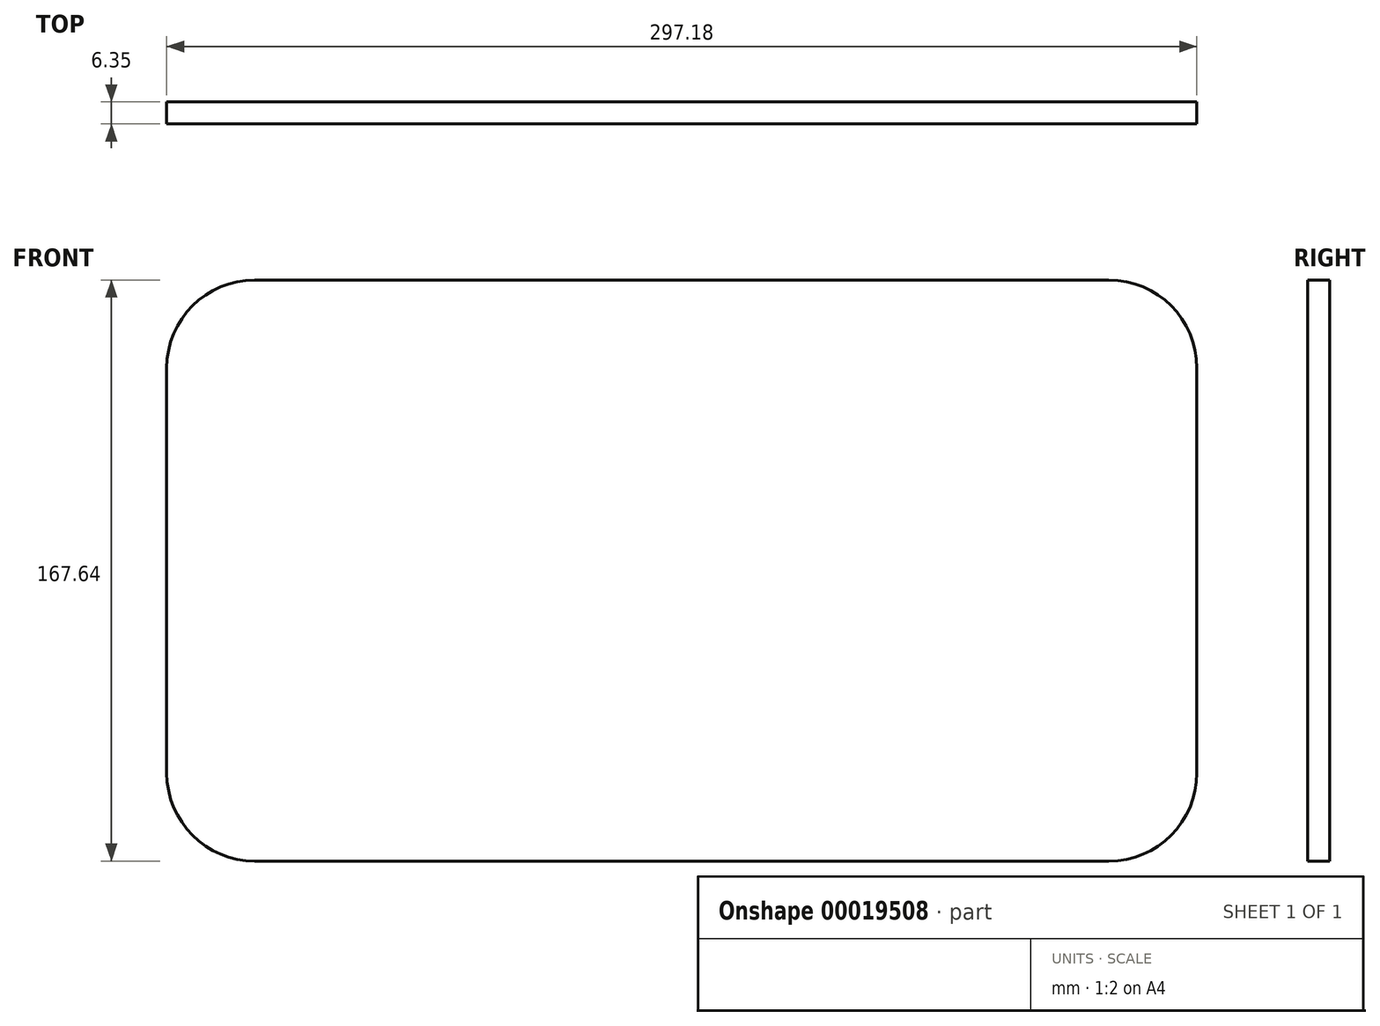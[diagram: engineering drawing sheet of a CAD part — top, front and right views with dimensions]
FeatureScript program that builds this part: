
annotation { "Feature Type Name" : "Feature", "Feature Type Description" : "" }
export const myFeature = defineFeature(function(context is Context, id is Id, definition is map)
    precondition{}
    {
        {
            var Q0;
            Q0=qCreatedBy(makeId("Front.planeOp"),FACE);
            var sketch = newSketch(context, id + "F0", { "sketchPlane" : qUnion([Q0])});
            skLineSegment(sketch, "E0.rect.bottom", {"start": v(148.6, 83.82) * mm, "end": v(-148.6, 83.82) * mm});
            skLineSegment(sketch, "E0.rect.top", {"start": v(148.6, -83.82) * mm, "end": v(-148.6, -83.82) * mm});
            skLineSegment(sketch, "E0.rect.left", {"start": v(148.6, 83.82) * mm, "end": v(148.6, -83.82) * mm});
            skLineSegment(sketch, "E0.rect.right", {"start": v(-148.6, 83.82) * mm, "end": v(-148.6, -83.82) * mm});
            skPoint(sketch, "E0.rect.middle", {"position": v(0, 0) * mm});
            skSolve(sketch);
        }
        {
            var Q0;
            Q0 = qSketchRegion(id + "F0", true);
            extrude(context, id + "F1", {"entities" : qUnion([Q0]), "depth" : 6.35 * mm});
        }
        {
            var Q0;
            Q0=makeQuery(id+"F1.opExtrude","SWEPT_EDGE",EDGE,{"disambiguationData":[OSD([sQuery(id+"F0.wireOp",EDGE,"E0.rect.bottom"),sQuery(id+"F0.wireOp",EDGE,"E0.rect.right")])]});
            var Q1;
            Q1=makeQuery(id+"F1.opExtrude","SWEPT_EDGE",EDGE,{"disambiguationData":[OSD([sQuery(id+"F0.wireOp",EDGE,"E0.rect.bottom"),sQuery(id+"F0.wireOp",EDGE,"E0.rect.left")])]});
            var Q2;
            Q2=makeQuery(id+"F1.opExtrude","SWEPT_EDGE",EDGE,{"disambiguationData":[OSD([sQuery(id+"F0.wireOp",EDGE,"E0.rect.top"),sQuery(id+"F0.wireOp",EDGE,"E0.rect.left")])]});
            var Q3;
            Q3=makeQuery(id+"F1.opExtrude","SWEPT_EDGE",EDGE,{"disambiguationData":[OSD([sQuery(id+"F0.wireOp",EDGE,"E0.rect.top"),sQuery(id+"F0.wireOp",EDGE,"E0.rect.right")])]});
            fillet(context, id + "F2", {"entities" : qUnion([Q0, Q1, Q2, Q3]), "radius" : 25.4 * mm, "tangentPropagation" : true, "allowEdgeOverflow" : false});
        }
    });
